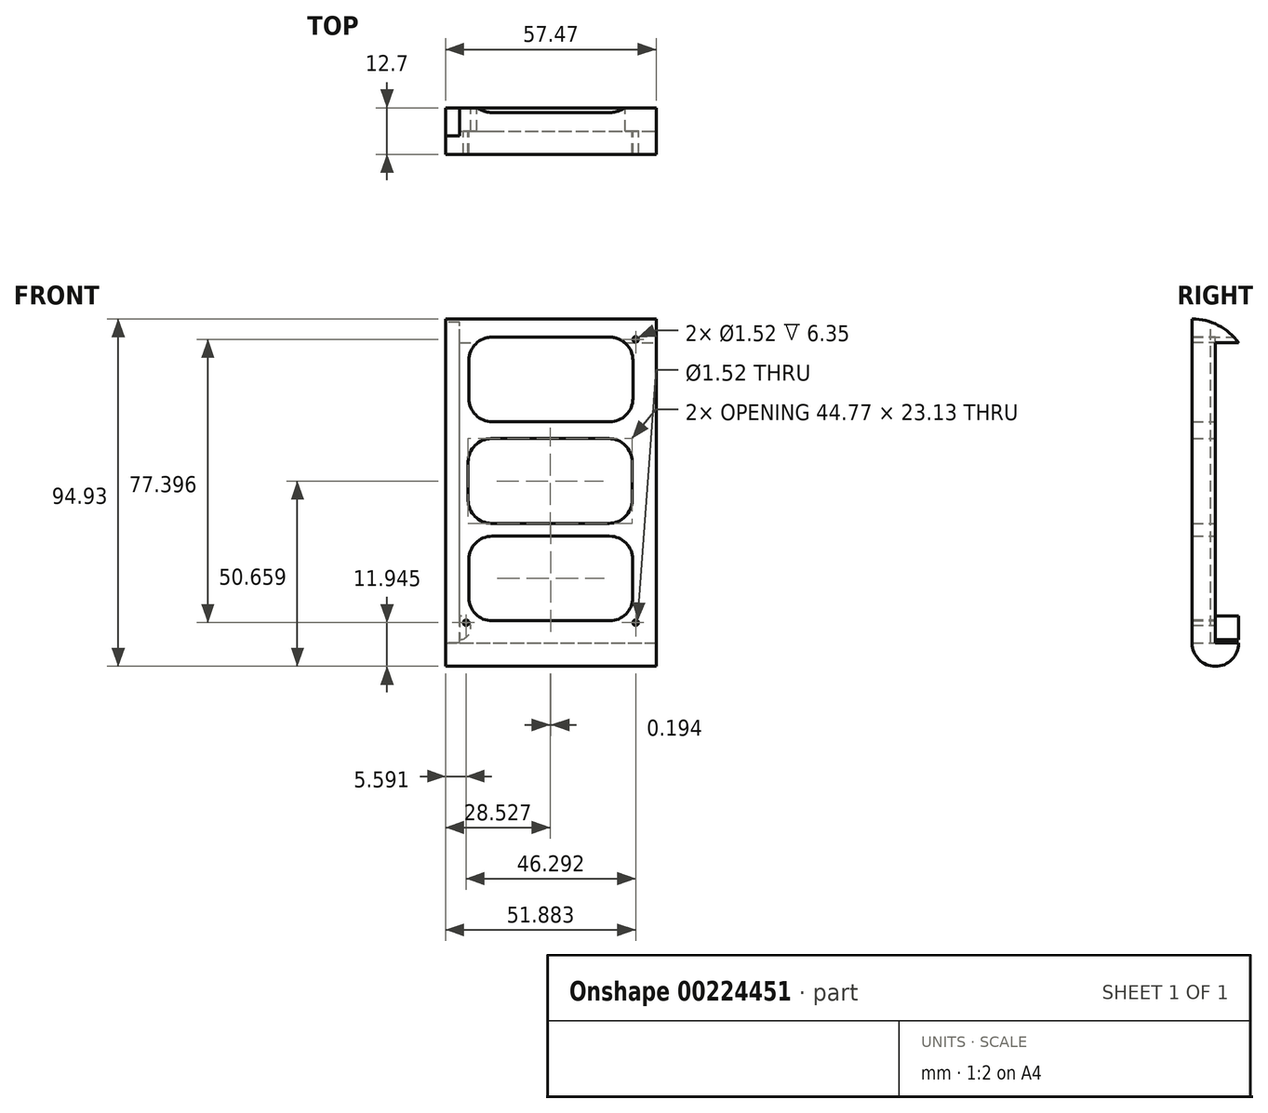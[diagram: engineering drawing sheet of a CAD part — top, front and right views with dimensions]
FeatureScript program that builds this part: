
annotation { "Feature Type Name" : "Feature", "Feature Type Description" : "" }
export const myFeature = defineFeature(function(context is Context, id is Id, definition is map)
    precondition{}
    {
        {
            var Q0;
            Q0=qCreatedBy(makeId("Front.planeOp"),FACE);
            var sketch = newSketch(context, id + "F0", { "sketchPlane" : qUnion([Q0])});
            skLineSegment(sketch, "E0.bottom", {"start": v(-20.07, 54.19) * mm, "end": v(37.4, 54.19) * mm});
            skLineSegment(sketch, "E0.top", {"start": v(-20.07, -34.4) * mm, "end": v(37.4, -34.4) * mm});
            skLineSegment(sketch, "E0.left", {"start": v(-20.07, 54.19) * mm, "end": v(-20.07, -34.4) * mm});
            skLineSegment(sketch, "E0.right", {"start": v(37.4, 54.19) * mm, "end": v(37.4, -34.4) * mm});
            skLineSegment(sketch, "E1.bottom", {"start": v(-7.37, 49.24) * mm, "end": v(24.7, 49.24) * mm});
            skLineSegment(sketch, "E1.top", {"start": v(-7.37, 26.1) * mm, "end": v(24.7, 26.1) * mm});
            skLineSegment(sketch, "E1.left", {"start": v(-13.72, 42.89) * mm, "end": v(-13.72, 32.46) * mm});
            skLineSegment(sketch, "E1.right", {"start": v(31.05, 42.89) * mm, "end": v(31.05, 32.46) * mm});
            skPoint(sketch, "E2.visualSharp", {"position": v(-13.72, 49.24) * mm});
            skArc(sketch, "E2.filletArc", {"start": v(-7.37, 49.24) * mm, "mid": v(-11.86, 47.38) * mm, "end": v(-13.72, 42.89) * mm});
            skPoint(sketch, "E3.visualSharp", {"position": v(-13.72, 26.1) * mm});
            skArc(sketch, "E3.filletArc", {"start": v(-13.72, 32.46) * mm, "mid": v(-11.86, 27.97) * mm, "end": v(-7.37, 26.1) * mm});
            skPoint(sketch, "E4.visualSharp", {"position": v(31.05, 26.1) * mm});
            skArc(sketch, "E4.filletArc", {"start": v(24.7, 26.1) * mm, "mid": v(29.2, 27.97) * mm, "end": v(31.05, 32.46) * mm});
            skPoint(sketch, "E5.visualSharp", {"position": v(31.05, 49.24) * mm});
            skArc(sketch, "E5.filletArc", {"start": v(31.05, 42.89) * mm, "mid": v(29.2, 47.38) * mm, "end": v(24.7, 49.24) * mm});
            skLineSegment(sketch, "E6.bottom", {"start": v(-7.58, 21.48) * mm, "end": v(24.5, 21.48) * mm});
            skLineSegment(sketch, "E6.top", {"start": v(-7.58, -1.65) * mm, "end": v(24.5, -1.65) * mm});
            skLineSegment(sketch, "E6.left", {"start": v(-13.93, 15.13) * mm, "end": v(-13.93, 4.7) * mm});
            skLineSegment(sketch, "E6.right", {"start": v(30.84, 15.13) * mm, "end": v(30.84, 4.7) * mm});
            skArc(sketch, "E7.filletArc", {"start": v(-7.58, 21.48) * mm, "mid": v(-12.07, 19.62) * mm, "end": v(-13.93, 15.13) * mm});
            skArc(sketch, "E8.filletArc", {"start": v(-13.93, 4.7) * mm, "mid": v(-12.07, 0.21) * mm, "end": v(-7.58, -1.65) * mm});
            skArc(sketch, "E9.filletArc", {"start": v(24.5, -1.65) * mm, "mid": v(28.98, 0.21) * mm, "end": v(30.84, 4.7) * mm});
            skArc(sketch, "E10.filletArc", {"start": v(30.84, 15.13) * mm, "mid": v(28.98, 19.62) * mm, "end": v(24.5, 21.48) * mm});
            skLineSegment(sketch, "E11.bottom", {"start": v(-7.38, -5.17) * mm, "end": v(24.68, -5.17) * mm});
            skLineSegment(sketch, "E11.top", {"start": v(-7.38, -28.3) * mm, "end": v(24.68, -28.3) * mm});
            skLineSegment(sketch, "E11.left", {"start": v(-13.73, -11.52) * mm, "end": v(-13.73, -21.95) * mm});
            skLineSegment(sketch, "E11.right", {"start": v(31.03, -11.52) * mm, "end": v(31.03, -21.95) * mm});
            skArc(sketch, "E12.filletArc", {"start": v(-7.38, -5.17) * mm, "mid": v(-11.87, -7.03) * mm, "end": v(-13.73, -11.52) * mm});
            skArc(sketch, "E13.filletArc", {"start": v(-13.73, -21.95) * mm, "mid": v(-11.87, -26.44) * mm, "end": v(-7.38, -28.3) * mm});
            skArc(sketch, "E14.filletArc", {"start": v(24.68, -28.3) * mm, "mid": v(29.17, -26.44) * mm, "end": v(31.03, -21.95) * mm});
            skArc(sketch, "E15.filletArc", {"start": v(31.03, -11.52) * mm, "mid": v(29.17, -7.03) * mm, "end": v(24.68, -5.17) * mm});
            skSolve(sketch);
        }
        {
            var Q0;
            Q0=makeQuery(id+"F0.imprint","IMPRINT",FACE,{"disambiguationData":[TD([[makeQuery(id+"F0.imprint","IMPRINT",EDGE,{"derivedFrom":sQuery(id+"F0.wireOp",EDGE,"E0.bottom")}),-1.0]])]});
            extrude(context, id + "F1", {"entities" : qUnion([Q0]), "depth" : 12.7 * mm});
        }
        {
            var Q0;
            Q0=makeQuery(id+"F1.opExtrude","SWEPT_FACE",FACE,{"disambiguationData":[OSD([sQuery(id+"F0.wireOp",EDGE,"E0.right")])]});
            var sketch = newSketch(context, id + "F2", { "sketchPlane" : qUnion([Q0])});
            skArc(sketch, "E16", {"start": v(0, 47.64) * mm, "mid": v(-5.56, 52.46) * mm, "end": v(-12.7, 54.19) * mm});
            skSolve(sketch);
        }
        {
            var Q0;
            {var subQ0=sQuery(id+"F2.wireOp",EDGE,"E16");Q0=makeQuery(id+"F2.imprint","IMPRINT",FACE,{"disambiguationData":[TD([[makeQuery(id+"F2.imprint","IMPRINT",EDGE,{"derivedFrom":subQ0}),-1.0]])]});}
            extrude(context, id + "F3", {"entities" : qUnion([Q0]), "operationType" : NewBodyOperationType.REMOVE, "endBound" : BoundingType.THROUGH_ALL, "oppositeDirection" : true, "depth" : 25.4 * mm});
        }
        {
            var Q0;
            Q0=makeQuery(id+"F1.opExtrude","CAP_FACE",FACE,{"disambiguationData":[OSD([sQuery(id+"F0.wireOp",EDGE,"E0.bottom"),sQuery(id+"F0.wireOp",EDGE,"E0.top"),sQuery(id+"F0.wireOp",EDGE,"E0.left"),sQuery(id+"F0.wireOp",EDGE,"E0.right"),sQuery(id+"F0.wireOp",EDGE,"E1.bottom"),sQuery(id+"F0.wireOp",EDGE,"E1.top"),sQuery(id+"F0.wireOp",EDGE,"E1.left"),sQuery(id+"F0.wireOp",EDGE,"E1.right"),sQuery(id+"F0.wireOp",EDGE,"E2.filletArc"),sQuery(id+"F0.wireOp",EDGE,"E3.filletArc"),sQuery(id+"F0.wireOp",EDGE,"E4.filletArc"),sQuery(id+"F0.wireOp",EDGE,"E5.filletArc"),sQuery(id+"F0.wireOp",EDGE,"E6.bottom"),sQuery(id+"F0.wireOp",EDGE,"E6.top"),sQuery(id+"F0.wireOp",EDGE,"E6.left"),sQuery(id+"F0.wireOp",EDGE,"E6.right"),sQuery(id+"F0.wireOp",EDGE,"E7.filletArc"),sQuery(id+"F0.wireOp",EDGE,"E8.filletArc"),sQuery(id+"F0.wireOp",EDGE,"E9.filletArc"),sQuery(id+"F0.wireOp",EDGE,"E10.filletArc"),sQuery(id+"F0.wireOp",EDGE,"E11.bottom"),sQuery(id+"F0.wireOp",EDGE,"E11.top"),sQuery(id+"F0.wireOp",EDGE,"E11.left"),sQuery(id+"F0.wireOp",EDGE,"E11.right"),sQuery(id+"F0.wireOp",EDGE,"E12.filletArc"),sQuery(id+"F0.wireOp",EDGE,"E13.filletArc"),sQuery(id+"F0.wireOp",EDGE,"E14.filletArc"),sQuery(id+"F0.wireOp",EDGE,"E15.filletArc")])],"isStart":false});
            var sketch = newSketch(context, id + "F4", { "sketchPlane" : qUnion([Q0])});
            skLineSegment(sketch, "E17.0", {"start": v(-16.51, 50.63) * mm, "end": v(33.84, 50.63) * mm});
            skLineSegment(sketch, "E17.1", {"start": v(-16.51, 50.63) * mm, "end": v(-16.51, -30.84) * mm});
            skLineSegment(sketch, "E17.2", {"start": v(-16.51, -30.84) * mm, "end": v(33.84, -30.84) * mm});
            skLineSegment(sketch, "E17.3", {"start": v(33.84, 50.63) * mm, "end": v(33.84, -30.84) * mm});
            skSolve(sketch);
        }
        {
            var Q0;
            Q0=makeQuery(id+"F4.imprint","IMPRINT",FACE,{"disambiguationData":[TD([[makeQuery(id+"F4.imprint","IMPRINT",EDGE,{"derivedFrom":sQuery(id+"F4.wireOp",EDGE,"E17.0")}),-1.0]])]});
            extrude(context, id + "F5", {"entities" : qUnion([Q0]), "operationType" : NewBodyOperationType.REMOVE, "oppositeDirection" : true, "depth" : 6.35 * mm});
        }
        {
            var Q0;
            Q0=makeQuery(id+"F5.boolean.opBoolean","COPY",FACE,{"derivedFrom":makeQuery(id+"F5.opExtrude","CAP_FACE",FACE,{"disambiguationData":[OSD([sQuery(id+"F0.wireOp",EDGE,"E1.bottom"),sQuery(id+"F0.wireOp",EDGE,"E1.top"),sQuery(id+"F0.wireOp",EDGE,"E1.left"),sQuery(id+"F0.wireOp",EDGE,"E1.right"),sQuery(id+"F0.wireOp",EDGE,"E2.filletArc"),sQuery(id+"F0.wireOp",EDGE,"E3.filletArc"),sQuery(id+"F0.wireOp",EDGE,"E4.filletArc"),sQuery(id+"F0.wireOp",EDGE,"E5.filletArc"),sQuery(id+"F0.wireOp",EDGE,"E6.bottom"),sQuery(id+"F0.wireOp",EDGE,"E6.top"),sQuery(id+"F0.wireOp",EDGE,"E6.left"),sQuery(id+"F0.wireOp",EDGE,"E6.right"),sQuery(id+"F0.wireOp",EDGE,"E7.filletArc"),sQuery(id+"F0.wireOp",EDGE,"E8.filletArc"),sQuery(id+"F0.wireOp",EDGE,"E9.filletArc"),sQuery(id+"F0.wireOp",EDGE,"E10.filletArc"),sQuery(id+"F0.wireOp",EDGE,"E11.bottom"),sQuery(id+"F0.wireOp",EDGE,"E11.top"),sQuery(id+"F0.wireOp",EDGE,"E11.left"),sQuery(id+"F0.wireOp",EDGE,"E11.right"),sQuery(id+"F0.wireOp",EDGE,"E12.filletArc"),sQuery(id+"F0.wireOp",EDGE,"E13.filletArc"),sQuery(id+"F0.wireOp",EDGE,"E14.filletArc"),sQuery(id+"F0.wireOp",EDGE,"E15.filletArc"),sQuery(id+"F4.wireOp",EDGE,"E17.0"),sQuery(id+"F4.wireOp",EDGE,"E17.1"),sQuery(id+"F4.wireOp",EDGE,"E17.2"),sQuery(id+"F4.wireOp",EDGE,"E17.3")])],"isStart":false})});
            var sketch = newSketch(context, id + "F6", { "sketchPlane" : qUnion([Q0])});
            skCircle(sketch, "E18", {"center": v(-14.48, 48.6) * mm, "radius": 0.76 * mm});
            skCircle(sketch, "E19", {"center": v(-14.48, -28.8) * mm, "radius": 0.76 * mm});
            skLineSegment(sketch, "E20", {"start": v(8.67, 50.63) * mm, "end": v(8.67, -30.84) * mm, "construction": true});
            skCircle(sketch, "E21.MirrorC", {"center": v(31.81, 48.6) * mm, "radius": 0.76 * mm});
            skCircle(sketch, "E22.MirrorC", {"center": v(31.81, -28.8) * mm, "radius": 0.76 * mm});
            skSolve(sketch);
        }
        {
            var Q0;
            Q0=makeQuery(id+"F6.imprint","IMPRINT",FACE,{"disambiguationData":[TD([[makeQuery(id+"F6.imprint","IMPRINT",EDGE,{"derivedFrom":sQuery(id+"F6.wireOp",EDGE,"E18")}),-1.0]])]});
            var sketch = newSketch(context, id + "F7", { "sketchPlane" : qUnion([Q0])});
            skSolve(sketch);
        }
        {
            var Q0;
            Q0=makeQuery(id+"F6.imprint","IMPRINT",FACE,{"disambiguationData":[TD([[makeQuery(id+"F6.imprint","IMPRINT",EDGE,{"derivedFrom":sQuery(id+"F6.wireOp",EDGE,"E18")}),1.0]])]});
            extrude(context, id + "F8", {"entities" : qUnion([Q0]), "operationType" : NewBodyOperationType.ADD, "depth" : 6.35 * mm});
        }
        {
            var Q0;
            Q0=makeQuery(id+"F7.imprint","IMPRINT",FACE,{"disambiguationData":[TD([[makeQuery(id+"F7.imprint","IMPRINT",EDGE,{"derivedFrom":makeQuery(id+"F6.imprint","IMPRINT",EDGE,{"derivedFrom":sQuery(id+"F6.wireOp",EDGE,"E21.MirrorC")})}),-1.0]])]});
            extrude(context, id + "F9", {"entities" : qUnion([Q0]), "operationType" : NewBodyOperationType.ADD, "depth" : 6.35 * mm});
        }
        {
            var Q0;
            Q0=makeQuery(id+"F1.opExtrude","SWEPT_FACE",FACE,{"disambiguationData":[OSD([sQuery(id+"F0.wireOp",EDGE,"E0.right")])]});
            var sketch = newSketch(context, id + "F10", { "sketchPlane" : qUnion([Q0])});
            skArc(sketch, "E23", {"start": v(-12.7, -34.4) * mm, "mid": v(-6.35, -40.74) * mm, "end": v(0, -34.4) * mm});
            skSolve(sketch);
        }
        {
            var Q0;
            Q0=makeQuery(id+"F10.imprint","IMPRINT",FACE,{"disambiguationData":[TD([[makeQuery(id+"F10.imprint","IMPRINT",EDGE,{"derivedFrom":sQuery(id+"F10.wireOp",EDGE,"E23")}),1.0]])]});
            extrude(context, id + "F11", {"entities" : qUnion([Q0]), "operationType" : NewBodyOperationType.ADD, "oppositeDirection" : true, "depth" : 56.4 * mm});
        }
        {
            var Q0;
            Q0=makeQuery(id+"F11.opExtrude","CAP_FACE",FACE,{"disambiguationData":[OSD([sQuery(id+"F0.wireOp",EDGE,"E0.top"),sQuery(id+"F0.wireOp",EDGE,"E0.right"),sQuery(id+"F10.wireOp",EDGE,"E23")])],"isStart":false});
            extrude(context, id + "F12", {"entities" : qUnion([Q0]), "operationType" : NewBodyOperationType.ADD, "depth" : 1.07 * mm});
        }
        {
            var Q0;
            Q0=makeQuery(id+"F1.opExtrude","SWEPT_FACE",FACE,{"disambiguationData":[OSD([sQuery(id+"F0.wireOp",EDGE,"E0.left")])]});
            var sketch = newSketch(context, id + "F13", { "sketchPlane" : qUnion([Q0])});
            skLineSegment(sketch, "E24", {"start": v(7.62, -34.4) * mm, "end": v(7.62, 53.34) * mm});
            skSolve(sketch);
        }
        {
            var Q0;
            Q0=makeQuery(id+"F1.opExtrude","CAP_FACE",FACE,{"disambiguationData":[OSD([sQuery(id+"F0.wireOp",EDGE,"E0.bottom"),sQuery(id+"F0.wireOp",EDGE,"E0.top"),sQuery(id+"F0.wireOp",EDGE,"E0.left"),sQuery(id+"F0.wireOp",EDGE,"E0.right"),sQuery(id+"F0.wireOp",EDGE,"E1.bottom"),sQuery(id+"F0.wireOp",EDGE,"E1.top"),sQuery(id+"F0.wireOp",EDGE,"E1.left"),sQuery(id+"F0.wireOp",EDGE,"E1.right"),sQuery(id+"F0.wireOp",EDGE,"E2.filletArc"),sQuery(id+"F0.wireOp",EDGE,"E3.filletArc"),sQuery(id+"F0.wireOp",EDGE,"E4.filletArc"),sQuery(id+"F0.wireOp",EDGE,"E5.filletArc"),sQuery(id+"F0.wireOp",EDGE,"E6.bottom"),sQuery(id+"F0.wireOp",EDGE,"E6.top"),sQuery(id+"F0.wireOp",EDGE,"E6.left"),sQuery(id+"F0.wireOp",EDGE,"E6.right"),sQuery(id+"F0.wireOp",EDGE,"E7.filletArc"),sQuery(id+"F0.wireOp",EDGE,"E8.filletArc"),sQuery(id+"F0.wireOp",EDGE,"E9.filletArc"),sQuery(id+"F0.wireOp",EDGE,"E10.filletArc"),sQuery(id+"F0.wireOp",EDGE,"E11.bottom"),sQuery(id+"F0.wireOp",EDGE,"E11.top"),sQuery(id+"F0.wireOp",EDGE,"E11.left"),sQuery(id+"F0.wireOp",EDGE,"E11.right"),sQuery(id+"F0.wireOp",EDGE,"E12.filletArc"),sQuery(id+"F0.wireOp",EDGE,"E13.filletArc"),sQuery(id+"F0.wireOp",EDGE,"E14.filletArc"),sQuery(id+"F0.wireOp",EDGE,"E15.filletArc")])],"isStart":true});
            var sketch = newSketch(context, id + "F14", { "sketchPlane" : qUnion([Q0])});
            skLineSegment(sketch, "E25", {"start": v(16.46, -34.4) * mm, "end": v(16.46, 47.64) * mm});
            skCircle(sketch, "E26", {"center": v(16.46, -30.2) * mm, "radius": 3.26 * mm});
            skSolve(sketch);
        }
        {
            var Q0;
            {var subQ0=sQuery(id+"F14.wireOp",EDGE,"E26");var subQ1=sQuery(id+"F14.wireOp",EDGE,"E25");var subQ2=makeQuery(id+"F14.imprint","INTERSECT",VERTEX,{"disambiguationData":[OD(0.0)],"derivedFrom":[subQ1,subQ0]});Q0=makeQuery(id+"F14.imprint","IMPRINT",FACE,{"disambiguationData":[TD([[makeQuery(id+"F14.imprint","IMPRINT",EDGE,{"disambiguationData":[TD([[subQ2,-1.0]])],"derivedFrom":subQ1}),-1.0]])]});}
            var Q1;
            {var subQ0=sQuery(id+"F14.wireOp",EDGE,"E26");var subQ1=sQuery(id+"F14.wireOp",EDGE,"E25");var subQ2=makeQuery(id+"F14.imprint","INTERSECT",VERTEX,{"disambiguationData":[OD(0.0)],"derivedFrom":[subQ1,subQ0]});Q1=makeQuery(id+"F14.imprint","IMPRINT",FACE,{"disambiguationData":[TD([[makeQuery(id+"F14.imprint","IMPRINT",EDGE,{"disambiguationData":[TD([[subQ2,-1.0]])],"derivedFrom":subQ1}),1.0]])]});}
            extrude(context, id + "F15", {"entities" : qUnion([Q0, Q1]), "operationType" : NewBodyOperationType.REMOVE, "oppositeDirection" : true, "depth" : 6.35 * mm});
        }
        {
            var Q0;
            {var subQ0=sQuery(id+"F13.wireOp",EDGE,"E24");Q0=makeQuery(id+"F13.imprint","IMPRINT",FACE,{"disambiguationData":[TD([[makeQuery(id+"F13.imprint","IMPRINT",EDGE,{"derivedFrom":subQ0}),1.0]])]});}
            extrude(context, id + "F16", {"entities" : qUnion([Q0]), "operationType" : NewBodyOperationType.REMOVE, "oppositeDirection" : true, "depth" : 3.8 * mm});
        }
    });
